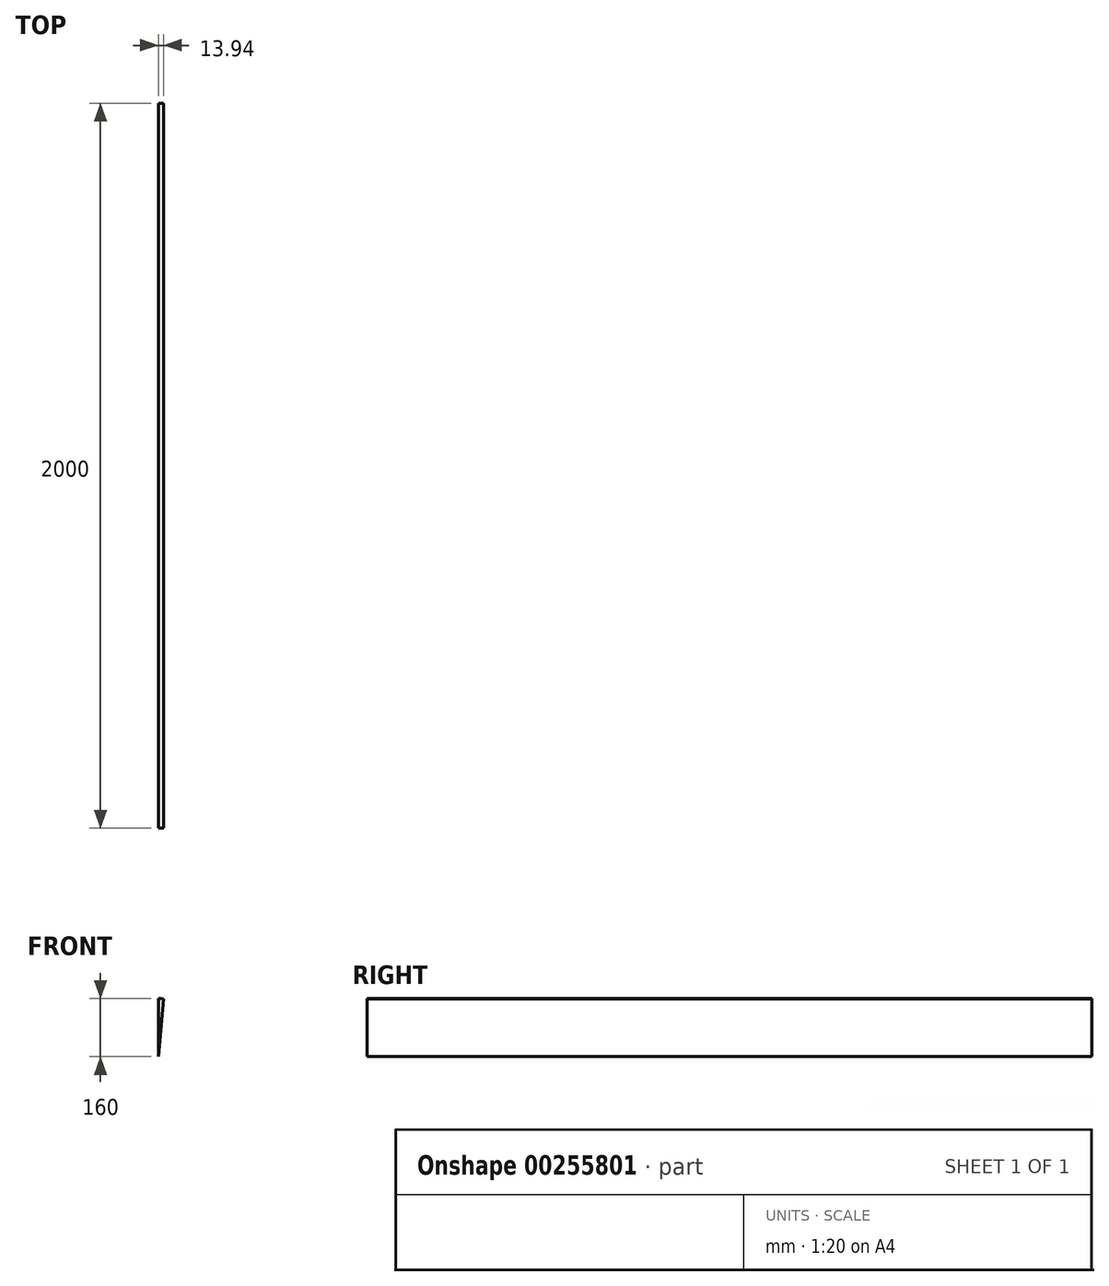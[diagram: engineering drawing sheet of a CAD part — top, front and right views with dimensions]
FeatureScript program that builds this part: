
annotation { "Feature Type Name" : "Feature", "Feature Type Description" : "" }
export const myFeature = defineFeature(function(context is Context, id is Id, definition is map)
    precondition{}
    {
        {
            var Q0;
            Q0=qCreatedBy(makeId("Front.planeOp"),FACE);
            var sketch = newSketch(context, id + "F0", { "sketchPlane" : qUnion([Q0])});
            skCircle(sketch, "E0", {"center": v(0, 0) * mm, "radius": 160 * mm});
            skLineSegment(sketch, "E1", {"start": v(0, 160) * mm, "end": v(0, 0) * mm});
            skLineSegment(sketch, "E2", {"start": v(0, 0) * mm, "end": v(13.94, 159.4) * mm});
            skSolve(sketch);
        }
        {
            var Q0;
            {var subQ0=sQuery(id+"F0.wireOp",EDGE,"E1");Q0=makeQuery(id+"F0.imprint","IMPRINT",FACE,{"disambiguationData":[TD([[makeQuery(id+"F0.imprint","IMPRINT",EDGE,{"derivedFrom":subQ0}),1.0]])]});}
            extrude(context, id + "F1", {"entities" : qUnion([Q0]), "depth" : 2000 * mm});
        }
    });
